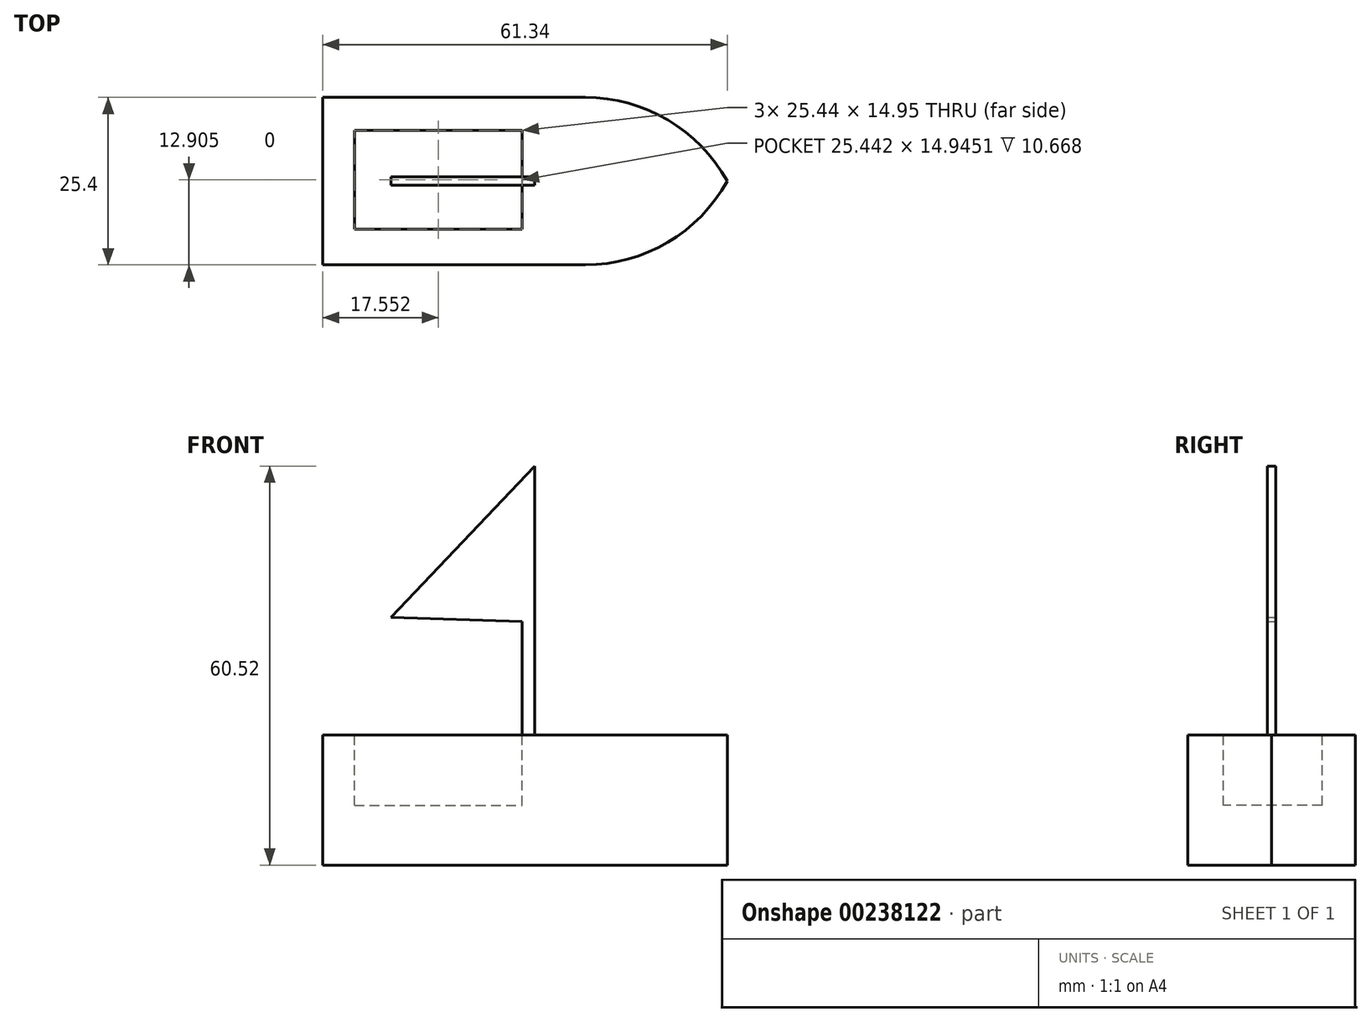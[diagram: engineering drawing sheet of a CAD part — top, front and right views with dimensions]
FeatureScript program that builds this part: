
annotation { "Feature Type Name" : "Feature", "Feature Type Description" : "" }
export const myFeature = defineFeature(function(context is Context, id is Id, definition is map)
    precondition{}
    {
        {
            var Q0;
            Q0=qCreatedBy(makeId("Front.planeOp"),FACE);
            var sketch = newSketch(context, id + "F0", { "sketchPlane" : qUnion([Q0])});
            skLineSegment(sketch, "E0.bottom", {"start": v(-30.26, 3.25) * mm, "end": v(34.12, 3.25) * mm});
            skLineSegment(sketch, "E0.top", {"start": v(-30.26, -16.45) * mm, "end": v(34.12, -16.45) * mm});
            skLineSegment(sketch, "E0.left", {"start": v(-30.26, 3.25) * mm, "end": v(-30.26, -16.45) * mm});
            skLineSegment(sketch, "E0.right", {"start": v(34.12, 3.25) * mm, "end": v(34.12, -16.45) * mm});
            skLineSegment(sketch, "E1", {"start": v(0, 3.25) * mm, "end": v(0, 20.51) * mm});
            skLineSegment(sketch, "E2", {"start": v(1.93, 3.25) * mm, "end": v(1.93, 44.07) * mm});
            skLineSegment(sketch, "E3", {"start": v(1.93, 44.07) * mm, "end": v(-19.9, 21.12) * mm});
            skLineSegment(sketch, "E4", {"start": v(-19.9, 21.12) * mm, "end": v(0, 20.51) * mm});
            skSolve(sketch);
        }
        {
            var Q0;
            Q0=makeQuery(id+"F0.imprint","IMPRINT",FACE,{"disambiguationData":[TD([[makeQuery(id+"F0.imprint","IMPRINT",EDGE,{"derivedFrom":sQuery(id+"F0.wireOp",EDGE,"E0.bottom")}),-1.0]])]});
            extrude(context, id + "F1", {"entities" : qUnion([Q0]), "endBound" : BoundingType.SYMMETRIC, "depth" : 25.4 * mm});
        }
        {
            var Q0;
            Q0=makeQuery(id+"F1.opExtrude","CAP_EDGE",EDGE,{"disambiguationData":[OSD([sQuery(id+"F0.wireOp",EDGE,"E0.right")])],"isStart":false});
            var Q1;
            Q1=makeQuery(id+"F1.opExtrude","CAP_EDGE",EDGE,{"disambiguationData":[OSD([sQuery(id+"F0.wireOp",EDGE,"E0.right")])],"isStart":true});
            fillet(context, id + "F2", {"entities" : qUnion([Q0, Q1]), "radius" : 24.53 * mm, "tangentPropagation" : true, "allowEdgeOverflow" : false});
        }
        {
            var Q0;
            {var subQ0=sQuery(id+"F0.wireOp",EDGE,"E1");Q0=makeQuery(id+"F0.imprint","IMPRINT",FACE,{"disambiguationData":[TD([[makeQuery(id+"F0.imprint","IMPRINT",EDGE,{"derivedFrom":subQ0}),-1.0]])]});}
            extrude(context, id + "F3", {"entities" : qUnion([Q0]), "endBound" : BoundingType.SYMMETRIC, "depth" : 1.27 * mm});
        }
        {
            var Q0;
            Q0=makeQuery(id+"F1.opExtrude","SWEPT_FACE",FACE,{"disambiguationData":[OSD([sQuery(id+"F0.wireOp",EDGE,"E0.bottom")])]});
            var sketch = newSketch(context, id + "F4", { "sketchPlane" : qUnion([Q0])});
            skLineSegment(sketch, "E5.bottom", {"start": v(-25.43, 7.68) * mm, "end": v(0.01, 7.68) * mm});
            skLineSegment(sketch, "E5.top", {"start": v(-25.43, -7.27) * mm, "end": v(0.01, -7.27) * mm});
            skLineSegment(sketch, "E5.left", {"start": v(-25.43, 7.68) * mm, "end": v(-25.43, -7.27) * mm});
            skLineSegment(sketch, "E5.right", {"start": v(0.01, 7.68) * mm, "end": v(0.01, -7.27) * mm});
            skSolve(sketch);
        }
        {
            var Q0;
            Q0=makeQuery(id+"F4.imprint","IMPRINT",FACE,{"disambiguationData":[TD([[makeQuery(id+"F4.imprint","IMPRINT",EDGE,{"derivedFrom":sQuery(id+"F4.wireOp",EDGE,"E5.bottom")}),-1.0]])]});
            extrude(context, id + "F5", {"entities" : qUnion([Q0]), "operationType" : NewBodyOperationType.REMOVE, "oppositeDirection" : true, "depth" : 10.67 * mm});
        }
    });
